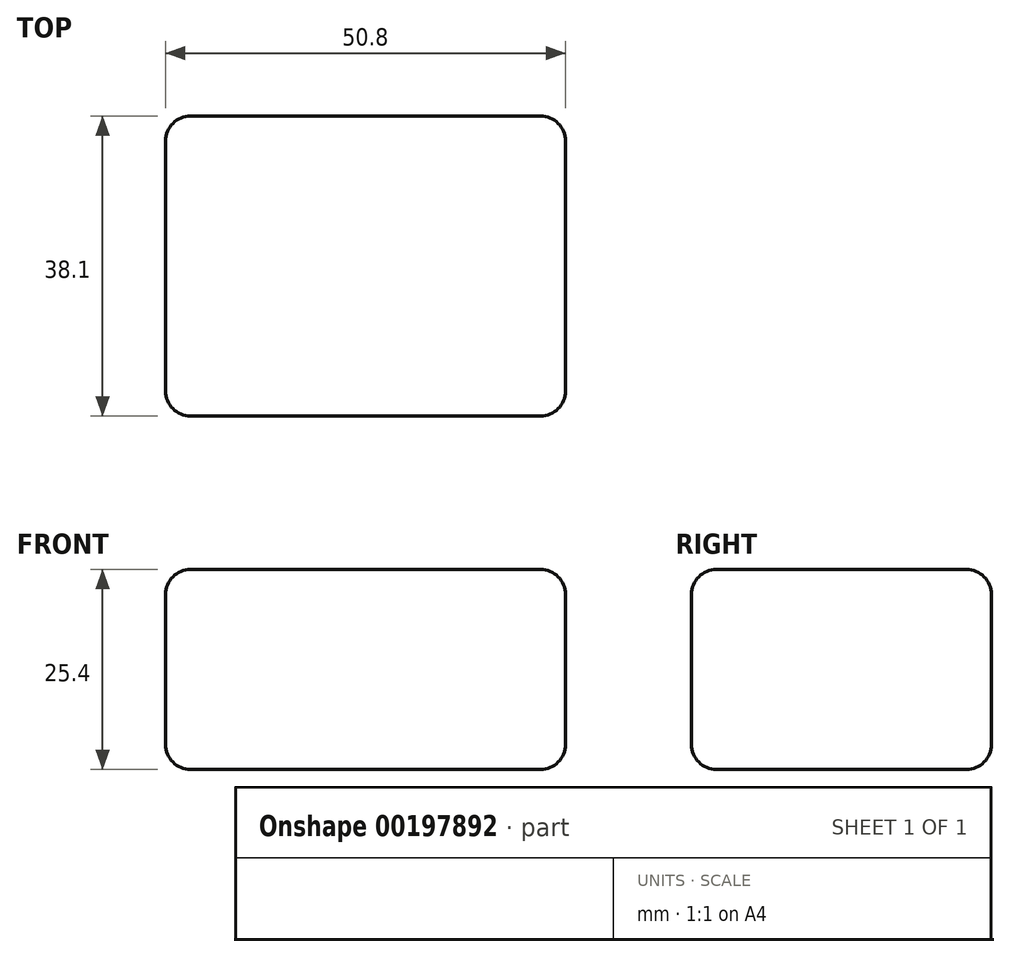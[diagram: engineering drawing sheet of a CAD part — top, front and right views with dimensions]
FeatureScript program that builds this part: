
annotation { "Feature Type Name" : "Feature", "Feature Type Description" : "" }
export const myFeature = defineFeature(function(context is Context, id is Id, definition is map)
    precondition{}
    {
        {
            var Q0;
            Q0=qCreatedBy(makeId("Top.planeOp"),FACE);
            var sketch = newSketch(context, id + "F0", { "sketchPlane" : qUnion([Q0])});
            skLineSegment(sketch, "E0.bottom", {"start": v(0, 0) * mm, "end": v(50.8, 0) * mm});
            skLineSegment(sketch, "E0.top", {"start": v(0, 38.1) * mm, "end": v(50.8, 38.1) * mm});
            skLineSegment(sketch, "E0.left", {"start": v(0, 0) * mm, "end": v(0, 38.1) * mm});
            skLineSegment(sketch, "E0.right", {"start": v(50.8, 0) * mm, "end": v(50.8, 38.1) * mm});
            skSolve(sketch);
        }
        {
            var Q0;
            Q0=makeQuery(id+"F0.imprint","IMPRINT",FACE,{"disambiguationData":[TD([[makeQuery(id+"F0.imprint","IMPRINT",EDGE,{"derivedFrom":sQuery(id+"F0.wireOp",EDGE,"E0.bottom")}),1.0]])]});
            extrude(context, id + "F1", {"entities" : qUnion([Q0]), "depth" : 25.4 * mm});
        }
        {
            var Q0;
            Q0=makeQuery(id+"F1.opExtrude","SWEPT_FACE",FACE,{"disambiguationData":[OSD([sQuery(id+"F0.wireOp",EDGE,"E0.left")])]});
            var Q1;
            Q1=makeQuery(id+"F1.opExtrude","SWEPT_FACE",FACE,{"disambiguationData":[OSD([sQuery(id+"F0.wireOp",EDGE,"E0.bottom")])]});
            var Q2;
            Q2=makeQuery(id+"F1.opExtrude","CAP_FACE",FACE,{"disambiguationData":[OSD([sQuery(id+"F0.wireOp",EDGE,"E0.bottom"),sQuery(id+"F0.wireOp",EDGE,"E0.top"),sQuery(id+"F0.wireOp",EDGE,"E0.left"),sQuery(id+"F0.wireOp",EDGE,"E0.right")])],"isStart":false});
            var Q3;
            Q3=makeQuery(id+"F1.opExtrude","SWEPT_FACE",FACE,{"disambiguationData":[OSD([sQuery(id+"F0.wireOp",EDGE,"E0.right")])]});
            var Q4;
            Q4=makeQuery(id+"F1.opExtrude","SWEPT_FACE",FACE,{"disambiguationData":[OSD([sQuery(id+"F0.wireOp",EDGE,"E0.top")])]});
            var Q5;
            Q5=makeQuery(id+"F1.opExtrude","CAP_FACE",FACE,{"disambiguationData":[OSD([sQuery(id+"F0.wireOp",EDGE,"E0.bottom"),sQuery(id+"F0.wireOp",EDGE,"E0.top"),sQuery(id+"F0.wireOp",EDGE,"E0.left"),sQuery(id+"F0.wireOp",EDGE,"E0.right")])],"isStart":true});
            fillet(context, id + "F2", {"entities" : qUnion([Q0, Q1, Q2, Q3, Q4, Q5]), "radius" : 3.17 * mm, "tangentPropagation" : true, "allowEdgeOverflow" : false});
        }
    });
